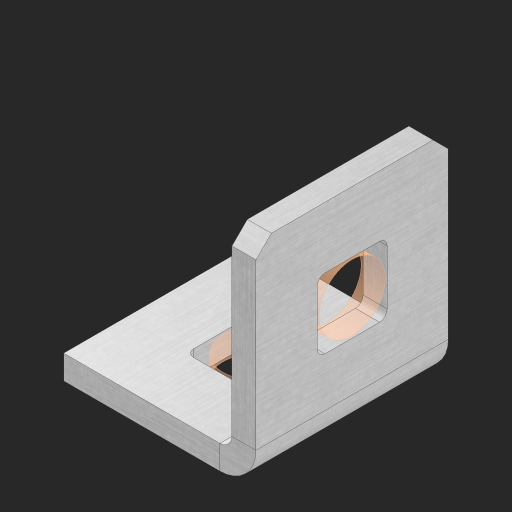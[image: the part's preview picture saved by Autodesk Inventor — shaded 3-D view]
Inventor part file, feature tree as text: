
AUTODESK INVENTOR PART (.ipt)
format: ipt  version: 2023 (Build 270158000, 158)  size: 525,824 bytes
history: native  units: in
note: dims shown in document units (in); Inventor stores cm internally (conversion verified against a paired STEP export)
features: other x75, extrude x69, sheet_metal_op x10, sketch x8, mirror x1, pattern_linear x1, chamfer x1
ambient origin geometry x8: Origin, YZ Plane, XZ Plane, XY Plane, X Axis, Y Axis, Z Axis, Center Point
bodies: Solid1 (feature_tree), Body (feature_tree)
feature tree (165):
  other  "Flange Pattern Plane"
  sheet_metal_op  "Flange Pattern"
  sheet_metal_op  "Body Pattern"
  other  "Arc Length"
  mirror  "Notch Mirror"
  pattern_linear  "Notch Pattern"  Spacing1=0.25in  [1 undecoded]
  chamfer  "End Chamfer"
  extrude  "Half Cut"  Depth=0.0625in
  sketch  "Sketch1"  dims[d0=1.5in]
  other  "Plate1"
  sketch  "Sketch2"  dims[d1=0.5in]
  other  "Plate2"
  sheet_metal_op  "Bend1"
  sheet_metal_op  "Corner1"
  sketch  "Sketch3"  dims[d2=0.0625in]
  other  "Flange Pattern Sketch"
  sketch  "Sketch7"  dims[d3=0.0625in]
  other  "Srf1"
  other  "Srf2"
  sketch  "Sketch8"  dims[d4=0.0312in]
  sketch  "Sketch9"  dims[d5=0.125in]
  other  "Srf91"
  sheet_metal_op  "Body Pattern Sketch"
  other  "Srf92"
  sketch  "Sketch13"  dims[d6=0.0625in]
  sketch  "Sketch14"  dims[d7=0.5in d8=90.0deg d9=0.0312in d10=0.25in d11=0.0625in d12=0.0625in d16=0.182in d17=0.02in d18=0.0625in d19=0.0in d20=0.25in d21=0.25in d46=0.172in d47=1.0in d48=0.0in d49=0.182in d50=0.02in d51=0.25in d52=0.25in d53=0.0625in d54=0.0in d55=0.172in d56=1.0in d57=0.0in d60=0.3937in d62=0.5in d63=0.3937in d65=0.5in d85=0.1473in d86=0.1782in d88=0.04in d89=0.0625in d90=0.0in d91=0.04in d92=0.0491in d95=2.5in d96=0.04in d97=0.25in d98=45.0deg d101=0.0in d102=2.497in d131=0.5in d132=0.3937in d134=0.5in d139=0.5in]
  other  "Srf856"
  other  "Srf1310"
  other  "Srf1311"
  other  "Srf1312"
  other  "Srf1376"
  other  "Srf1377"
  other  "Srf1728"
  other  "Srf1755"
  other  "Srf1878"
  other  "Srf1879"
  other  "Srf1880"
  other  "Srf1881"
  other  "Srf1882"
  other  "Srf1883"
  other  "Srf1884"
  other  "Srf1885"
  other  "Srf1886"
  other  "Srf1887"
  other  "Srf1888"
  other  "Srf1889"
  other  "Srf1890"
  other  "Srf1891"
  other  "Srf1892"
  other  "Srf1893"
  other  "Srf1894"
  other  "Srf1895"
  other  "Srf1896"
  other  "Srf1897"
  other  "Srf1898"
  other  "Srf1899"
  other  "Srf1900"
  other  "Srf1901"
  other  "Srf1902"
  other  "Srf1903"
  other  "Srf1904"
  other  "Srf1905"
  other  "Srf1906"
  other  "Srf1942"
  other  "Srf1943"
  other  "Srf1944"
  other  "Srf1945"
  other  "Srf1946"
  other  "Srf1947"
  other  "Srf1948"
  other  "Srf1949"
  other  "Srf1950"
  other  "Srf1951"
  other  "Srf1952"
  other  "Srf1953"
  other  "Srf1954"
  other  "Srf1955"
  other  "Srf1956"
  other  "Srf1957"
  other  "Srf1958"
  other  "Srf1959"
  other  "Srf1960"
  other  "Srf1961"
  other  "Srf1962"
  other  "Srf1963"
  other  "Srf1964"
  other  "Srf1965"
  other  "Srf1966"
  other  "Srf1967"
  other  "Srf1968"
  other  "Srf1969"
  other  "Srf1970"
  sheet_metal_op  "Flange Stamp"
  sheet_metal_op  "Flange Circle"
  sheet_metal_op  "Body Stamp"
  sheet_metal_op  "Body Circle"
  sheet_metal_op  "Notch"
  extrude  "ExtrusionSrf2"  Depth=0.0625in
  extrude  "ExtrusionSrf92"  Depth=0.182in
  extrude  "ExtrusionSrf856"  Depth=0.02in
  extrude  "ExtrusionSrf1310"  Depth=0.0625in
  extrude  "ExtrusionSrf1311"  TaperAngle=0.0deg  [1 undecoded]
  extrude  "ExtrusionSrf1312"  Depth=0.25in
  extrude  "ExtrusionSrf1376"  Depth=0.25in
  extrude  "ExtrusionSrf1377"  Depth=0.5in
  extrude  "ExtrusionSrf1728"  Depth=0.5in TaperAngle=0.0deg
  extrude  "ExtrusionSrf1755"  Depth=0.182in
  extrude  "ExtrusionSrf1878"  Depth=0.02in
  extrude  "ExtrusionSrf1879"  Depth=0.25in
  extrude  "ExtrusionSrf1880"  Depth=0.25in
  extrude  "ExtrusionSrf1881"  Depth=0.0625in
  extrude  "ExtrusionSrf1882"  TaperAngle=0.0deg  [1 undecoded]
  extrude  "ExtrusionSrf1883"  Depth=0.5in
  extrude  "ExtrusionSrf1884"  Depth=0.5in TaperAngle=0.0deg
  extrude  "ExtrusionSrf1885"  Depth=0.3937in
  extrude  "ExtrusionSrf1886"  Depth=0.5in
  extrude  "ExtrusionSrf1887"  Depth=0.5in
  extrude  "ExtrusionSrf1888"  Depth=0.5in
  extrude  "ExtrusionSrf1889"  Depth=0.5in
  extrude  "ExtrusionSrf1890"  Depth=0.0625in
  extrude  "ExtrusionSrf1891"  TaperAngle=0.0deg  [1 undecoded]
  extrude  "ExtrusionSrf1892"  Depth=0.5in
  extrude  "ExtrusionSrf1893"  Depth=0.5in
  extrude  "ExtrusionSrf1894"  Depth=0.5in
  extrude  "ExtrusionSrf1895"  Depth=0.25in TaperAngle=45.0deg
  extrude  "ExtrusionSrf1896"  TaperAngle=0.0deg  [1 undecoded]
  extrude  "ExtrusionSrf1897"  Depth=0.5in
  extrude  "ExtrusionSrf1898"  Depth=0.5in
  extrude  "ExtrusionSrf1899"  Depth=0.3937in
  extrude  "ExtrusionSrf1900"  Depth=0.5in
  extrude  "ExtrusionSrf1901"  Depth=0.5in
  extrude  "ExtrusionSrf1902"  [1 undecoded]
  extrude  "ExtrusionSrf1903"  [1 undecoded]
  extrude  "ExtrusionSrf1904"  [1 undecoded]
  extrude  "ExtrusionSrf1905"  [1 undecoded]
  extrude  "ExtrusionSrf1906"  [1 undecoded]
  extrude  "ExtrusionSrf1942"  [1 undecoded]
  extrude  "ExtrusionSrf1943"  [1 undecoded]
  extrude  "ExtrusionSrf1944"  [1 undecoded]
  extrude  "ExtrusionSrf1945"  [1 undecoded]
  extrude  "ExtrusionSrf1946"  [1 undecoded]
  extrude  "ExtrusionSrf1947"  [1 undecoded]
  extrude  "ExtrusionSrf1948"  [1 undecoded]
  extrude  "ExtrusionSrf1949"  [1 undecoded]
  extrude  "ExtrusionSrf1950"  [1 undecoded]
  extrude  "ExtrusionSrf1951"  [1 undecoded]
  extrude  "ExtrusionSrf1952"  [1 undecoded]
  extrude  "ExtrusionSrf1953"  [1 undecoded]
  extrude  "ExtrusionSrf1954"  [1 undecoded]
  extrude  "ExtrusionSrf1955"  [1 undecoded]
  extrude  "ExtrusionSrf1956"  [1 undecoded]
  extrude  "ExtrusionSrf1957"  [1 undecoded]
  extrude  "ExtrusionSrf1958"  [1 undecoded]
  extrude  "ExtrusionSrf1959"  [1 undecoded]
  extrude  "ExtrusionSrf1960"  [1 undecoded]
  extrude  "ExtrusionSrf1961"  [1 undecoded]
  extrude  "ExtrusionSrf1962"  [1 undecoded]
  extrude  "ExtrusionSrf1963"  [1 undecoded]
  extrude  "ExtrusionSrf1964"  [1 undecoded]
  extrude  "ExtrusionSrf1965"  [1 undecoded]
  extrude  "ExtrusionSrf1966"  [1 undecoded]
  extrude  "ExtrusionSrf1967"  [1 undecoded]
  extrude  "ExtrusionSrf1968"  [1 undecoded]
  extrude  "ExtrusionSrf1969"  [1 undecoded]
  extrude  "ExtrusionSrf1970"  [1 undecoded]
note: 39 required parameter values undecoded (feature->parameter linkage not recoverable at this tier; creation-order binding heuristic only, values carry confidence <= 0.55)
